# Revit family: AM 900 VM
name_source: partatom
category: Mechanical Equipment
units: mm (PartAtom-declared; Revit-internal decimal feet)

## family parameters
Always vertical = Yes
Cut with Voids When Loaded = No
OmniClass Number = 23.75.00.00
OmniClass Title = Climate Control (HVAC)
Part Type = Normal
Room Calculation Point = No
Round Connector Dimension = Use Diameter
Shared = No
Work Plane-Based = No

## types (1)
- AM 900 VM
    BMS IN = (PTS) 2x2x0,6
    BMS Out = (PTS) 2x2x0,6
    BMS Panel = (PTS) 2x2x0,6
    Condensate = 9 mm  [stored 0.0295276 ft]
    Condensate conector = Ø6/9 mm
    Electrical connection = 1 ~ 230 V / N / PE / 50 Hz
    Exhaust Air = 315 mm
    Manufacturer = Airmaster A/S
    Max. flow rate 30 dB(A) with ePM10 50% filters = 980 m³
    Max. flow rate 30 dB(A) with ePM10 55% filters = 882 m³
    Max. flow rate 30 dB(A) with ePM10 80% filters = 784 m³
    Max. flow rate 35 dB(A) with ePM10 50% filters = 1260 m³
    Max. flow rate 35 dB(A) with ePM10 55% filters = 1134 m³
    Max. flow rate 35 dB(A) with ePM10 80% filters = 1008 m³
    Model = AM 900 VM
    Network Conection = AWG 24 CAT 5e STP
    Nominal current, air handling unit = 1,8 A
    Nominal current, electrical comfort heating surface = 4,4 A
    Nominal current, electrical preheating surface = 6,5 A
    Phase 1 - Max Current = 12,7A
    Phase 1 - Max Power Consumption = 2.790 w
    Suply Air In = 315 mm
    Total Depth = 602 mm  [stored 1.97507 ft]
    Total Hight = 2323 mm  [stored 7.62139 ft]
    Total Width = 800 mm  [stored 2.62467 ft]
    URL = www.airmaster-as.com
    Water Heater Surface IN = 15 mm  [stored 0.0492126 ft]
    Water Heater Surface Return = 15 mm  [stored 0.0492126 ft]
    Water heating surface Return = 1/2" (DN 15)
    Water heating surface in = 1/2" (DN 15)
    Weight (Standard Unit) = 301.5

note: [stored X ft] marks values corroborated as IEEE doubles in the binary element streams (Revit-internal decimal feet)

## geometry (parser evidence)
native form markers: Sweep x6
no freeform markers — native parametric forms only
